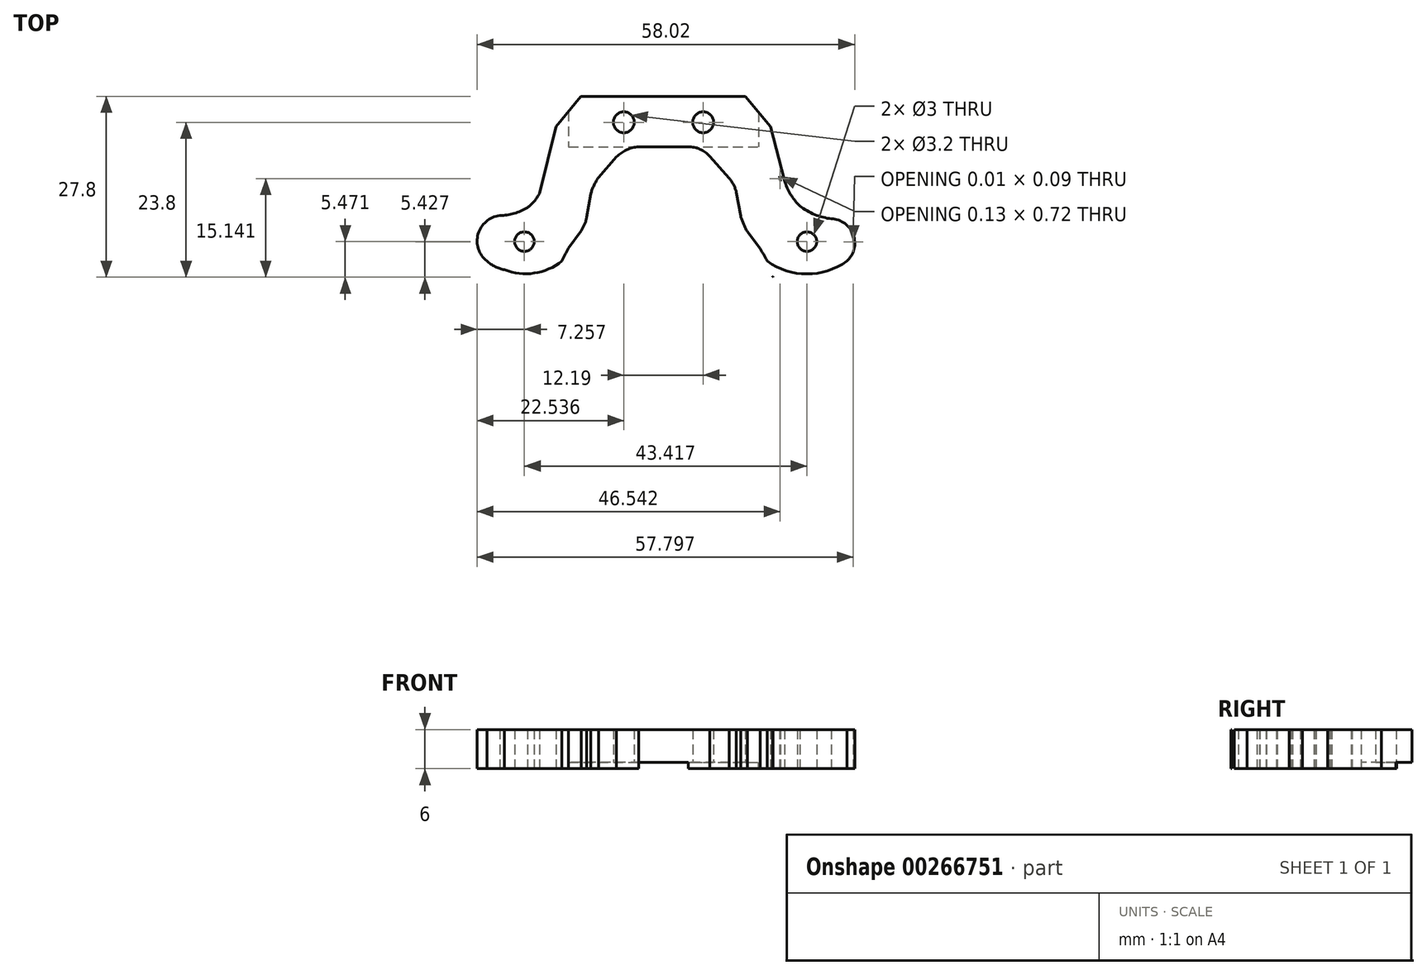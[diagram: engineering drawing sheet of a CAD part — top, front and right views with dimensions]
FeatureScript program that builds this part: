
annotation { "Feature Type Name" : "Feature", "Feature Type Description" : "" }
export const myFeature = defineFeature(function(context is Context, id is Id, definition is map)
    precondition{}
    {
        {
            var Q0;
            Q0=qCreatedBy(makeId("Top.planeOp"),FACE);
            var sketch = newSketch(context, id + "F0", { "sketchPlane" : qUnion([Q0])});
            skLineSegment(sketch, "E0.top", {"start": v(-35.25, 26) * mm, "end": v(-10, 26) * mm});
            skPoint(sketch, "E1.orphan", {"position": v(0, 26) * mm});
            skPoint(sketch, "E2.end.orphan", {"position": v(-5.25, 26) * mm});
            skPoint(sketch, "E3.end.orphan", {"position": v(-35.25, 26) * mm});
            skPoint(sketch, "E4.end.orphan", {"position": v(-38, 7.17) * mm});
            skLineSegment(sketch, "E5", {"start": v(-39.06, 21.32) * mm, "end": v(-35.25, 26) * mm});
            skPoint(sketch, "E6.orphan", {"position": v(-3.5, 7.17) * mm});
            skPoint(sketch, "E7.orphan", {"position": v(-7, 7.17) * mm});
            skLineSegment(sketch, "E8", {"start": v(-4.71, 13.7) * mm, "end": v(-4.58, 12.98) * mm});
            skPoint(sketch, "E9.start.orphan", {"position": v(-7, 26) * mm});
            skPoint(sketch, "E10.orphan", {"position": v(-38.25, 26) * mm});
            skLineSegment(sketch, "E11.right", {"start": v(6.6, 3.67) * mm, "end": v(6.6, 3.58) * mm});
            skLineSegment(sketch, "E12", {"start": v(-26.37, 18.22) * mm, "end": v(-18.77, 18.22) * mm});
            skLineSegment(sketch, "E13", {"start": v(-15.46, 16.79) * mm, "end": v(-12.45, 13.4) * mm});
            skLineSegment(sketch, "E14", {"start": v(-32.53, 13.54) * mm, "end": v(-29.78, 16.68) * mm});
            skLineSegment(sketch, "E15", {"start": v(-33.74, 11) * mm, "end": v(-34.35, 7.46) * mm});
            skLineSegment(sketch, "E16", {"start": v(-11.38, 11.25) * mm, "end": v(-10.7, 7.62) * mm});
            skLineSegment(sketch, "E17", {"start": v(-37.17, 2.67) * mm, "end": v(-35.2, 5.34) * mm});
            skLineSegment(sketch, "E18", {"start": v(-9.67, 5.18) * mm, "end": v(-7.72, 2.59) * mm});
            skPoint(sketch, "E19.orphan", {"position": v(-9.29, 0) * mm});
            skPoint(sketch, "E20.orphan", {"position": v(-35.63, 0) * mm});
            skPoint(sketch, "E21.start.orphan", {"position": v(-45, 7.17) * mm});
            skArc(sketch, "E22", {"start": v(-4.71, 13.7) * mm, "mid": v(-4.66, 13.34) * mm, "end": v(-4.58, 12.98) * mm});
            skArc(sketch, "E23", {"start": v(-47.72, 7.68) * mm, "mid": v(-45.52, 8) * mm, "end": v(-43.48, 8.89) * mm});
            skPoint(sketch, "E24.orphan", {"position": v(-41.5, 7.17) * mm});
            skPoint(sketch, "E25.orphan", {"position": v(0, 7.17) * mm});
            skArc(sketch, "E26", {"start": v(-32.53, 13.54) * mm, "mid": v(-33.24, 12.32) * mm, "end": v(-33.74, 11) * mm});
            skPoint(sketch, "E27.orphan", {"position": v(-33.48, 12.45) * mm});
            skArc(sketch, "E28", {"start": v(-26.37, 18.22) * mm, "mid": v(-28.22, 17.76) * mm, "end": v(-29.78, 16.68) * mm});
            skPoint(sketch, "E29.orphan", {"position": v(-28.43, 18.22) * mm});
            skArc(sketch, "E30", {"start": v(-15.46, 16.79) * mm, "mid": v(-16.97, 17.85) * mm, "end": v(-18.77, 18.22) * mm});
            skPoint(sketch, "E31.orphan", {"position": v(-16.74, 18.22) * mm});
            skArc(sketch, "E32", {"start": v(-11.32, 10.96) * mm, "mid": v(-11.71, 12.26) * mm, "end": v(-12.45, 13.4) * mm});
            skPoint(sketch, "E33.orphan", {"position": v(-11.6, 12.44) * mm});
            skArc(sketch, "E34", {"start": v(-10.7, 7.62) * mm, "mid": v(-10.26, 6.37) * mm, "end": v(-9.67, 5.18) * mm});
            skPoint(sketch, "E35.orphan", {"position": v(-10.44, 6.22) * mm});
            skArc(sketch, "E36", {"start": v(-35.2, 5.34) * mm, "mid": v(-34.67, 6.36) * mm, "end": v(-34.35, 7.46) * mm});
            skPoint(sketch, "E37.orphan", {"position": v(-34.56, 6.22) * mm});
            skArc(sketch, "E38", {"start": v(-7.73, 2.6) * mm, "mid": v(-7.73, 2.59) * mm, "end": v(-7.72, 2.59) * mm});
            skPoint(sketch, "E39.orphan", {"position": v(-5.79, 0) * mm});
            skPoint(sketch, "E40.orphan", {"position": v(-39.13, 0) * mm});
            skPoint(sketch, "E41.orphan", {"position": v(-51.5, 7.17) * mm});
            skArc(sketch, "E42", {"start": v(-5.78, -1.65) * mm, "mid": v(-5.76, -1.72) * mm, "end": v(-5.74, -1.8) * mm});
            skArc(sketch, "E43", {"start": v(-5.74, -1.8) * mm, "mid": v(-5.76, -1.72) * mm, "end": v(-5.78, -1.65) * mm});
            skPoint(sketch, "E44.orphan", {"position": v(-1.68, -4.07) * mm});
            skArc(sketch, "E45", {"start": v(-37.17, 2.67) * mm, "mid": v(-37.7, 1.68) * mm, "end": v(-38.17, 0.67) * mm});
            skPoint(sketch, "E46.orphan", {"position": v(-41.5, -4.07) * mm});
            skPoint(sketch, "E47.orphan", {"position": v(-43.22, -4.07) * mm});
            skArc(sketch, "E48", {"start": v(6.6, 3.58) * mm, "mid": v(6.6, 3.63) * mm, "end": v(6.61, 3.67) * mm});
            skPoint(sketch, "E49.orphan", {"position": v(6.5, 7.17) * mm});
            skPoint(sketch, "E50.centerSnap0", {"position": v(-51.6, 2.1) * mm});
            skLineSegment(sketch, "E51", {"start": v(-6.14, 21.32) * mm, "end": v(-10, 26) * mm});
            skPoint(sketch, "E52.end.orphan", {"position": v(-5.88, 21.32) * mm});
            skPoint(sketch, "E53.orphan", {"position": v(-44.94, -4.07) * mm});
            skPoint(sketch, "E0.bottom.start.orphan", {"position": v(-44.94, 0) * mm});
            skPoint(sketch, "E54.top.end.orphan", {"position": v(-51.63, 0) * mm});
            skArc(sketch, "E55.trimOffspring", {"start": v(-6.65, 0.67) * mm, "mid": v(-7.15, 1.65) * mm, "end": v(-7.72, 2.59) * mm});
            skPoint(sketch, "E11.top.start.orphan", {"position": v(0, 0) * mm});
            skPoint(sketch, "E56.trimOffspring.start.orphan", {"position": v(-3.36, 0) * mm});
            skPoint(sketch, "E57.orphan", {"position": v(-3.36, -4.07) * mm});
            skPoint(sketch, "E58.end.orphan", {"position": v(6.71, 0) * mm});
            skPoint(sketch, "E58.start.orphan", {"position": v(0, -4.07) * mm});
            skArc(sketch, "E59", {"start": v(-47, -0.66) * mm, "mid": v(-42.4, -1.18) * mm, "end": v(-38.17, 0.67) * mm});
            skArc(sketch, "E60", {"start": v(-50.32, 1.28) * mm, "mid": v(-48.82, 0.04) * mm, "end": v(-47, -0.66) * mm});
            skPoint(sketch, "E61.centerSnap0", {"position": v(-43.93, 0.67) * mm});
            skPoint(sketch, "E62.centerSnap0", {"position": v(-0.52, 0.67) * mm});
            skPoint(sketch, "E62.perimeterSnap0", {"position": v(-0.52, 0.67) * mm});
            skPoint(sketch, "E62.perimeterSnap1", {"position": v(-36.19, 4) * mm});
            skCircle(sketch, "E63", {"center": v(-43.93, 3.67) * mm, "radius": 1.5 * mm});
            skCircle(sketch, "E64", {"center": v(-0.52, 3.67) * mm, "radius": 1.5 * mm});
            skArc(sketch, "E65", {"start": v(-6.65, 0.67) * mm, "mid": v(-0.52, -1.3) * mm, "end": v(5.62, 0.67) * mm});
            skPoint(sketch, "E66.orphan", {"position": v(4.33, -0.8) * mm});
            skPoint(sketch, "E67.start.orphan", {"position": v(-49.7, 0.67) * mm});
            skLineSegment(sketch, "E68.trimOffspring", {"start": v(6.58, 3.67) * mm, "end": v(6.61, 3.67) * mm});
            skArc(sketch, "E69", {"start": v(-47.72, 7.68) * mm, "mid": v(-51.04, 4.83) * mm, "end": v(-49.7, 0.67) * mm});
            skPoint(sketch, "E54.right.end.orphan", {"position": v(-51.57, 3.58) * mm});
            skPoint(sketch, "E54.right.start.orphan", {"position": v(-51.56, 4.2) * mm});
            skArc(sketch, "E70", {"start": v(-1.63, 9.16) * mm, "mid": v(0.67, 7.83) * mm, "end": v(3.25, 7.17) * mm});
            skArc(sketch, "E71", {"start": v(5.62, 0.67) * mm, "mid": v(6.6, 4.7) * mm, "end": v(3.25, 7.17) * mm});
            skLineSegment(sketch, "E72", {"start": v(-39.06, 21.32) * mm, "end": v(-41.63, 11.04) * mm});
            skArc(sketch, "E73", {"start": v(-43.48, 8.89) * mm, "mid": v(-42.43, 9.86) * mm, "end": v(-41.63, 11.04) * mm});
            skPoint(sketch, "E74.start.orphan", {"position": v(-40.28, 14.24) * mm});
            skLineSegment(sketch, "E75", {"start": v(-6.14, 21.32) * mm, "end": v(-3.95, 13.04) * mm});
            skPoint(sketch, "E76.start.orphan", {"position": v(-5.93, 20.23) * mm});
            skArc(sketch, "E77", {"start": v(-4.03, 13.34) * mm, "mid": v(-3.12, 11.08) * mm, "end": v(-1.63, 9.16) * mm});
            skPoint(sketch, "E77.startSnap0", {"position": v(-4.65, 13.34) * mm});
            skPoint(sketch, "E78.orphan", {"position": v(-3.4, 10.96) * mm});
            skSolve(sketch);
        }
        {
            var Q0;
            Q0 = qSketchRegion(id + "F0", true);
            extrude(context, id + "F1", {"entities" : qUnion([Q0]), "depth" : 6 * mm});
        }
        {
            var Q0;
            Q0=makeQuery(id+"F1.opExtrude","CAP_FACE",FACE,{"disambiguationData":[OSD([sQuery(id+"F0.wireOp",EDGE,"E0.top"),sQuery(id+"F0.wireOp",EDGE,"E74"),sQuery(id+"F0.wireOp",EDGE,"E5"),sQuery(id+"F0.wireOp",EDGE,"dBJT8Cw2-kiiE-JVtB-cWXl-Jo8WRkg6q42H"),sQuery(id+"F0.wireOp",EDGE,"E8"),sQuery(id+"F0.wireOp",EDGE,"E54.right"),sQuery(id+"F0.wireOp",EDGE,"E11.right"),sQuery(id+"F0.wireOp",EDGE,"E12"),sQuery(id+"F0.wireOp",EDGE,"E13"),sQuery(id+"F0.wireOp",EDGE,"E14"),sQuery(id+"F0.wireOp",EDGE,"E15"),sQuery(id+"F0.wireOp",EDGE,"E16"),sQuery(id+"F0.wireOp",EDGE,"E17"),sQuery(id+"F0.wireOp",EDGE,"E18"),sQuery(id+"F0.wireOp",EDGE,"9pgpmbjm-VHAV-VmKi-r7EP-zy3Ju1hnVyc4"),sQuery(id+"F0.wireOp",EDGE,"E22"),sQuery(id+"F0.wireOp",EDGE,"rj1mGid4-xFnT-5L7G-8oH3-5rQVDscBIdu8"),sQuery(id+"F0.wireOp",EDGE,"E23"),sQuery(id+"F0.wireOp",EDGE,"E26"),sQuery(id+"F0.wireOp",EDGE,"E28"),sQuery(id+"F0.wireOp",EDGE,"E30"),sQuery(id+"F0.wireOp",EDGE,"E32"),sQuery(id+"F0.wireOp",EDGE,"E34"),sQuery(id+"F0.wireOp",EDGE,"E36"),sQuery(id+"F0.wireOp",EDGE,"E38"),sQuery(id+"F0.wireOp",EDGE,"7pML4YSL-yiDA-D2yh-V960-KRGg61vCjFmG"),sQuery(id+"F0.wireOp",EDGE,"IGeuu9I0-9ooR-3LEY-gD5L-lz7DSk6ZP3Wm"),sQuery(id+"F0.wireOp",EDGE,"ArIczMb2-31dy-rm4w-YmVm-JGPmwflz5pzP"),sQuery(id+"F0.wireOp",EDGE,"E42"),sQuery(id+"F0.wireOp",EDGE,"5CBCV5pV-P6g0-NZko-TJbt-ypDVxmAhKuvs"),sQuery(id+"F0.wireOp",EDGE,"E43"),sQuery(id+"F0.wireOp",EDGE,"E45"),sQuery(id+"F0.wireOp",EDGE,"E48"),sQuery(id+"F0.wireOp",EDGE,"E58"),sQuery(id+"F0.wireOp",EDGE,"0UirUm4J-w40v-Yv3M-HN0D-oRn1FItKkyv0")])],"isStart":true});
            var sketch = newSketch(context, id + "F2", { "sketchPlane" : qUnion([Q0])});
            skPoint(sketch, "E79.firstSnap0", {"position": v(-37.15, -23.66) * mm});
            skPoint(sketch, "E79.oppositeSnap0", {"position": v(-7.96, -23.12) * mm});
            skLineSegment(sketch, "E79.bottom", {"start": v(-37.15, -26.33) * mm, "end": v(-7.96, -26.33) * mm});
            skLineSegment(sketch, "E79.left", {"start": v(-37.15, -26.33) * mm, "end": v(-37.15, -18.22) * mm});
            skLineSegment(sketch, "E79.right", {"start": v(-7.96, -26.33) * mm, "end": v(-7.96, -18.22) * mm});
            skLineSegment(sketch, "E80", {"start": v(-37.15, -18.22) * mm, "end": v(-7.96, -18.22) * mm});
            skPoint(sketch, "E81.orphan", {"position": v(-7.96, -14.58) * mm});
            skSolve(sketch);
        }
        {
            var Q0;
            Q0 = qSketchRegion(id + "F2", true);
            extrude(context, id + "F3", {"entities" : qUnion([Q0]), "operationType" : NewBodyOperationType.REMOVE, "oppositeDirection" : true, "depth" : 1 * mm});
        }
        {
            var Q0;
            Q0=makeQuery(id+"F3.boolean.opBoolean","COPY",FACE,{"derivedFrom":makeQuery(id+"F3.opExtrude","CAP_FACE",FACE,{"disambiguationData":[OSD([sQuery(id+"F2.wireOp",EDGE,"E79.bottom"),sQuery(id+"F2.wireOp",EDGE,"E79.top"),sQuery(id+"F2.wireOp",EDGE,"E79.left"),sQuery(id+"F2.wireOp",EDGE,"E79.right")])],"isStart":false})});
            var sketch = newSketch(context, id + "F4", { "sketchPlane" : qUnion([Q0])});
            skCircle(sketch, "E82", {"center": v(-28.65, -22) * mm, "radius": 1.6 * mm});
            skCircle(sketch, "E83", {"center": v(-16.46, -22) * mm, "radius": 1.6 * mm});
            skSolve(sketch);
        }
        {
            var Q0;
            Q0 = qSketchRegion(id + "F4", true);
            extrude(context, id + "F5", {"entities" : qUnion([Q0]), "operationType" : NewBodyOperationType.REMOVE, "oppositeDirection" : true, "depth" : 25 * mm});
        }
    });
